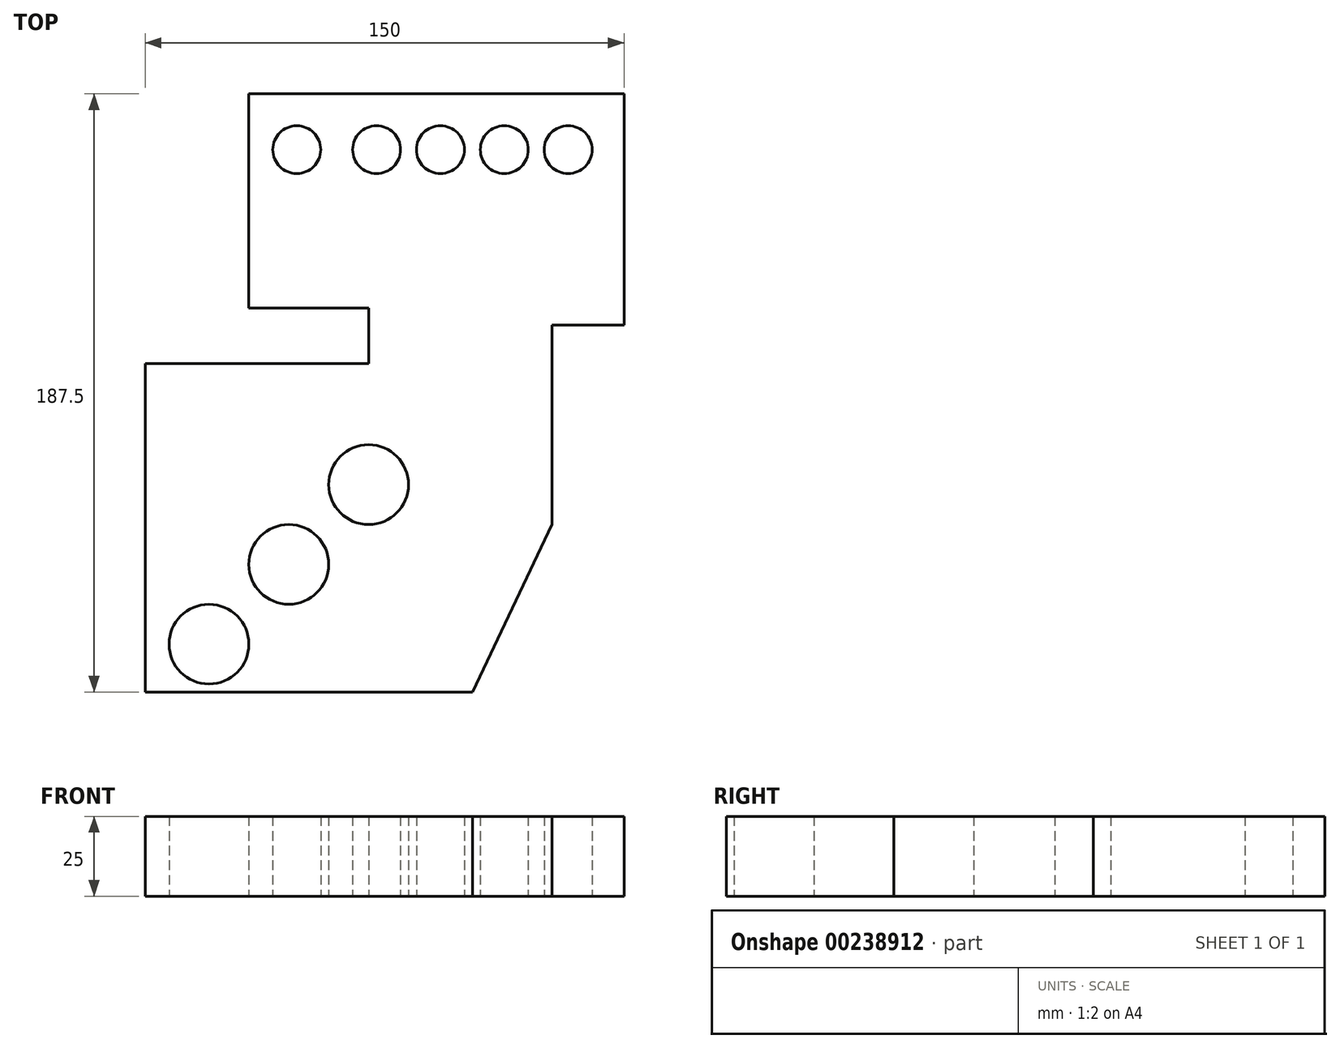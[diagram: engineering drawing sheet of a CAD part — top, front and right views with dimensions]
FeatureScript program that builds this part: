
annotation { "Feature Type Name" : "Feature", "Feature Type Description" : "" }
export const myFeature = defineFeature(function(context is Context, id is Id, definition is map)
    precondition{}
    {
        {
            var Q0;
            Q0=qCreatedBy(makeId("Top.planeOp"),FACE);
            var sketch = newSketch(context, id + "F0", { "sketchPlane" : qUnion([Q0])});
            skLineSegment(sketch, "E0", {"start": v(-70, -12.08) * mm, "end": v(-70, -115) * mm});
            skLineSegment(sketch, "E1", {"start": v(-70, -115) * mm, "end": v(32.5, -115) * mm});
            skLineSegment(sketch, "E2", {"start": v(32.5, -115) * mm, "end": v(57.5, -62.5) * mm});
            skLineSegment(sketch, "E3", {"start": v(57.5, -62.5) * mm, "end": v(57.5, 0) * mm});
            skLineSegment(sketch, "E4", {"start": v(57.5, 0) * mm, "end": v(80, 0) * mm});
            skLineSegment(sketch, "E5", {"start": v(80, 0) * mm, "end": v(80, 72.5) * mm});
            skLineSegment(sketch, "E6", {"start": v(80, 72.5) * mm, "end": v(-37.5, 72.5) * mm});
            skLineSegment(sketch, "E7", {"start": v(-37.5, 72.5) * mm, "end": v(-37.5, 5.42) * mm});
            skLineSegment(sketch, "E8", {"start": v(-37.5, 5.42) * mm, "end": v(0, 5.42) * mm});
            skLineSegment(sketch, "E9", {"start": v(0, 5.42) * mm, "end": v(0, -12.08) * mm});
            skLineSegment(sketch, "E10", {"start": v(-70, -12.08) * mm, "end": v(0, -12.08) * mm});
            skCircle(sketch, "E11", {"center": v(-50, -100) * mm, "radius": 12.5 * mm});
            skCircle(sketch, "E12", {"center": v(-25, -75) * mm, "radius": 12.5 * mm});
            skCircle(sketch, "E13", {"center": v(0, -50) * mm, "radius": 12.5 * mm});
            skCircle(sketch, "E14", {"center": v(62.5, 55) * mm, "radius": 7.5 * mm});
            skCircle(sketch, "E15", {"center": v(42.5, 55) * mm, "radius": 7.5 * mm});
            skCircle(sketch, "E16", {"center": v(22.5, 55) * mm, "radius": 7.5 * mm});
            skCircle(sketch, "E17", {"center": v(2.5, 55) * mm, "radius": 7.5 * mm});
            skCircle(sketch, "E18", {"center": v(-22.5, 55) * mm, "radius": 7.5 * mm});
            skSolve(sketch);
        }
        {
            var Q0;
            Q0 = qSketchRegion(id + "F0", true);
            var Q1;
            Q1=makeQuery(id+"F0.imprint","IMPRINT",FACE,{"disambiguationData":[TD([[makeQuery(id+"F0.imprint","IMPRINT",EDGE,{"derivedFrom":sQuery(id+"F0.wireOp",EDGE,"E0")}),1.0]])]});
            extrude(context, id + "F1", {"entities" : qUnion([Q0, Q1]), "depth" : 25 * mm});
        }
    });
